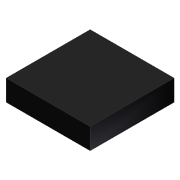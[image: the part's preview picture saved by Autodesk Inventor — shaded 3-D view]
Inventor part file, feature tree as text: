
AUTODESK INVENTOR PART (.ipt)
format: ipt  version: unknown  size: 165,888 bytes
history: native  units: mm
features: extrude x1, sketch x1
ambient origin geometry x8: Origin, YZ Plane, XZ Plane, XY Plane, X Axis, Y Axis, Z Axis, Center Point
feature tree (2):
  extrude  "Выдавливание2"  Depth=6.0mm
  sketch  "Эскиз2"
